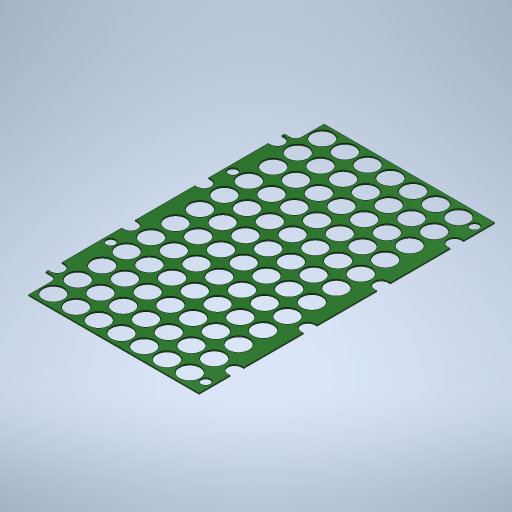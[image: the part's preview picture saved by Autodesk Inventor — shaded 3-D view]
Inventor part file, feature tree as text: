
AUTODESK INVENTOR PART (.ipt)
format: ipt  version: 2024 (Build 280153000, 153)  size: 554,496 bytes
history: native  units: mm
features: extrude x1, sketch x1
ambient origin geometry x8: Origin, YZ Plane, XZ Plane, XY Plane, X Axis, Y Axis, Z Axis, Center Point
bodies: Body1 (feature_tree)
feature tree (2):
  extrude  "Extrusion3"  Depth=1.0mm
  sketch  "Skizze3"  dims[d21=1.0mm d22=0.0mm d49=7.0mm d50=3.0mm d51=10.75mm]
